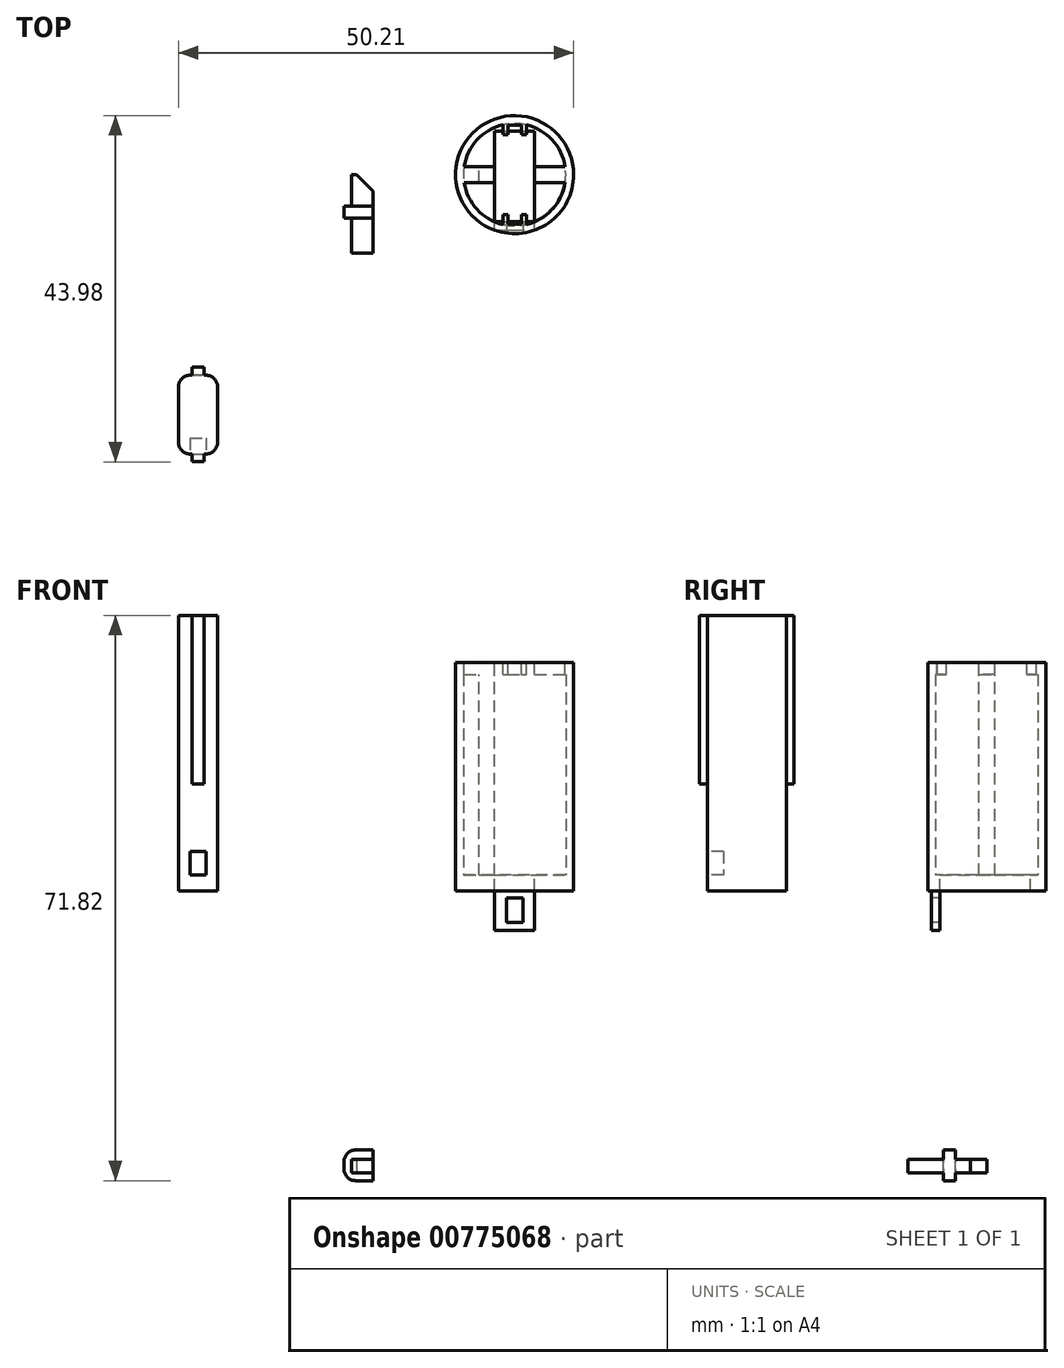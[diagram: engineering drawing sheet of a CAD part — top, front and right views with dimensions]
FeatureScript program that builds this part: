
annotation { "Feature Type Name" : "Feature", "Feature Type Description" : "" }
export const myFeature = defineFeature(function(context is Context, id is Id, definition is map)
    precondition{}
    {
        {
            var Q0;
            Q0=qCreatedBy(makeId("Top.planeOp"),FACE);
            var sketch = newSketch(context, id + "F0", { "sketchPlane" : qUnion([Q0])});
            skCircle(sketch, "E0", {"center": v(0, 0) * mm, "radius": 7.5 * mm});
            skSolve(sketch);
        }
        {
            var Q0;
            Q0=qSketchRegion(id+"F0",true);
            extrude(context, id + "F1", {"entities" : qUnion([Q0]), "depth" : 29 * mm});
        }
        {
            var Q0;
            Q0=qCreatedBy(makeId("Top.planeOp"),FACE);
            var sketch = newSketch(context, id + "F2", { "sketchPlane" : qUnion([Q0])});
            skCircle(sketch, "E1", {"center": v(0, 0) * mm, "radius": 6.5 * mm});
            skSolve(sketch);
        }
        {
            var Q0;
            Q0=makeQuery(id+"F2.imprint","IMPRINT",FACE,{"disambiguationData":[TD([[makeQuery(id+"F2.imprint","IMPRINT",EDGE,{"derivedFrom":sQuery(id+"F2.wireOp",EDGE,"E1")}),1.0]])]});
            extrude(context, id + "F3", {"entities" : qUnion([Q0]), "operationType" : NewBodyOperationType.REMOVE, "depth" : 30 * mm});
        }
        {
            var Q0;
            Q0=makeQuery(id+"F1.opExtrude","CAP_FACE",FACE,{"disambiguationData":[OSD([sQuery(id+"F0.wireOp",EDGE,"E0")])],"isStart":true});
            var sketch = newSketch(context, id + "F4", { "sketchPlane" : qUnion([Q0])});
            skCircle(sketch, "E2", {"center": v(0, 0) * mm, "radius": 6.5 * mm});
            skSolve(sketch);
        }
        {
            var Q0;
            Q0=makeQuery(id+"F4.imprint","IMPRINT",FACE,{"disambiguationData":[TD([[makeQuery(id+"F4.imprint","IMPRINT",EDGE,{"derivedFrom":sQuery(id+"F4.wireOp",EDGE,"E2")}),-1.0]])]});
            extrude(context, id + "F5", {"entities" : qUnion([Q0]), "operationType" : NewBodyOperationType.ADD, "oppositeDirection" : true, "depth" : 2 * mm});
        }
        {
            var Q0;
            Q0=qCreatedBy(makeId("Top.planeOp"),FACE);
            var sketch = newSketch(context, id + "F6", { "sketchPlane" : qUnion([Q0])});
            skLineSegment(sketch, "E3.bottom", {"start": v(-42.71, -35.48) * mm, "end": v(-40.96, -35.48) * mm});
            skLineSegment(sketch, "E3.top", {"start": v(-42.71, -25.48) * mm, "end": v(-40.96, -25.48) * mm});
            skLineSegment(sketch, "E3.left", {"start": v(-42.71, -35.48) * mm, "end": v(-42.71, -25.48) * mm});
            skLineSegment(sketch, "E3.right", {"start": v(-37.71, -35.48) * mm, "end": v(-37.71, -25.48) * mm});
            skLineSegment(sketch, "E4.top", {"start": v(-40.96, -24.48) * mm, "end": v(-39.46, -24.48) * mm});
            skLineSegment(sketch, "E4.left", {"start": v(-40.96, -25.48) * mm, "end": v(-40.96, -24.48) * mm});
            skLineSegment(sketch, "E4.right", {"start": v(-39.46, -25.48) * mm, "end": v(-39.46, -24.48) * mm});
            skLineSegment(sketch, "E5.top", {"start": v(-40.96, -36.48) * mm, "end": v(-39.46, -36.48) * mm});
            skLineSegment(sketch, "E5.left", {"start": v(-40.96, -35.48) * mm, "end": v(-40.96, -36.48) * mm});
            skLineSegment(sketch, "E5.right", {"start": v(-39.46, -35.48) * mm, "end": v(-39.46, -36.48) * mm});
            skLineSegment(sketch, "E6.trimOffspring", {"start": v(-39.46, -25.48) * mm, "end": v(-37.71, -25.48) * mm});
            skLineSegment(sketch, "E7.trimOffspring", {"start": v(-39.46, -35.48) * mm, "end": v(-37.71, -35.48) * mm});
            skSolve(sketch);
        }
        {
            var Q0;
            Q0=qSketchRegion(id+"F6",true);
            extrude(context, id + "F7", {"entities" : qUnion([Q0]), "depth" : 35 * mm});
        }
        {
            var Q0;
            Q0=makeQuery(id+"F1.opExtrude","CAP_FACE",FACE,{"disambiguationData":[OSD([sQuery(id+"F0.wireOp",EDGE,"E0")])],"isStart":false});
            var sketch = newSketch(context, id + "F8", { "sketchPlane" : qUnion([Q0])});
            skLineSegment(sketch, "E8.bottom", {"start": v(-6.5, 1) * mm, "end": v(-2.55, 1) * mm});
            skLineSegment(sketch, "E8.top", {"start": v(-6.5, -1) * mm, "end": v(-2.55, -1) * mm});
            skLineSegment(sketch, "E8.left", {"start": v(-6.5, 1) * mm, "end": v(-6.5, -1) * mm});
            skLineSegment(sketch, "E8.right", {"start": v(-2.55, 1) * mm, "end": v(-2.55, -1) * mm});
            skLineSegment(sketch, "E9.bottom", {"start": v(2.55, 1) * mm, "end": v(6.5, 1) * mm});
            skLineSegment(sketch, "E9.top", {"start": v(2.55, -1) * mm, "end": v(6.5, -1) * mm});
            skLineSegment(sketch, "E9.left", {"start": v(2.55, 1) * mm, "end": v(2.55, -1) * mm});
            skLineSegment(sketch, "E9.right", {"start": v(6.5, 1) * mm, "end": v(6.5, -1) * mm});
            skLineSegment(sketch, "E10", {"start": v(2.7, -7) * mm, "end": v(-8.3, -7) * mm});
            skPoint(sketch, "E11", {"position": v(-6.5, 0) * mm});
            skPoint(sketch, "E12", {"position": v(6.5, 0) * mm});
            skArc(sketch, "E13.trimOffspring", {"start": v(5.92, -1) * mm, "mid": v(6, 0) * mm, "end": v(5.92, 1) * mm});
            skArc(sketch, "E14.trimOffspring", {"start": v(-5.92, 1) * mm, "mid": v(-6, 0) * mm, "end": v(-5.92, -1) * mm});
            skLineSegment(sketch, "E15.bottom", {"start": v(-1.5, -6.5) * mm, "end": v(1.5, -6.5) * mm});
            skLineSegment(sketch, "E15.top", {"start": v(-1.5, -5.1) * mm, "end": v(-0.85, -5.1) * mm});
            skLineSegment(sketch, "E15.left", {"start": v(-1.5, -6.5) * mm, "end": v(-1.5, -5.1) * mm});
            skLineSegment(sketch, "E15.right", {"start": v(1.5, -6.5) * mm, "end": v(1.5, -5.1) * mm});
            skLineSegment(sketch, "E16.bottom", {"start": v(-1.5, 6.5) * mm, "end": v(1.5, 6.5) * mm});
            skLineSegment(sketch, "E16.top", {"start": v(-1.5, 5.1) * mm, "end": v(-0.85, 5.1) * mm});
            skLineSegment(sketch, "E16.left", {"start": v(-1.5, 6.5) * mm, "end": v(-1.5, 5.1) * mm});
            skLineSegment(sketch, "E16.right", {"start": v(1.5, 6.5) * mm, "end": v(1.5, 5.1) * mm});
            skPoint(sketch, "E17", {"position": v(0, 6.5) * mm});
            skPoint(sketch, "E18", {"position": v(0, -6.5) * mm});
            skLineSegment(sketch, "E19.top", {"start": v(-0.85, 6.3) * mm, "end": v(0.85, 6.3) * mm});
            skLineSegment(sketch, "E19.left", {"start": v(-0.85, 5.1) * mm, "end": v(-0.85, 6.3) * mm});
            skLineSegment(sketch, "E19.right", {"start": v(0.85, 5.1) * mm, "end": v(0.85, 6.3) * mm});
            skLineSegment(sketch, "E20.top", {"start": v(-0.85, -6.3) * mm, "end": v(0.85, -6.3) * mm});
            skLineSegment(sketch, "E20.left", {"start": v(-0.85, -5.1) * mm, "end": v(-0.85, -6.3) * mm});
            skLineSegment(sketch, "E20.right", {"start": v(0.85, -5.1) * mm, "end": v(0.85, -6.3) * mm});
            skLineSegment(sketch, "E21.trimOffspring", {"start": v(0.85, 5.1) * mm, "end": v(1.5, 5.1) * mm});
            skLineSegment(sketch, "E22.trimOffspring", {"start": v(0.85, -5.1) * mm, "end": v(1.5, -5.1) * mm});
            skSolve(sketch);
        }
        {
            var Q0;
            {var subQ4=sQuery(id+"F8.wireOp",EDGE,"E8.right");Q0=makeQuery(id+"F8.imprint","IMPRINT",FACE,{"disambiguationData":[TD([[makeQuery(id+"F8.imprint","IMPRINT",EDGE,{"derivedFrom":subQ4}),-1.0]])]});}
            var Q1;
            {var subQ1=sQuery(id+"F8.wireOp",EDGE,"XQCQReMM-DMfq-NEXw-nXjC-cKNYx5jDkKxh.top");Q1=makeQuery(id+"F8.imprint","IMPRINT",FACE,{"disambiguationData":[TD([[makeQuery(id+"F8.imprint","IMPRINT",EDGE,{"derivedFrom":subQ1}),1.0]])]});}
            var Q2;
            {var subQ0=sQuery(id+"F8.wireOp",EDGE,"E9.left");Q2=makeQuery(id+"F8.imprint","IMPRINT",FACE,{"disambiguationData":[TD([[makeQuery(id+"F8.imprint","IMPRINT",EDGE,{"derivedFrom":subQ0}),1.0]])]});}
            var Q3;
            {var subQ0=sQuery(id+"F8.wireOp",EDGE,"yVMaH1Gn-iFFF-JhyI-hApD-2K1NMgFAN3S1.top");Q3=makeQuery(id+"F8.imprint","IMPRINT",FACE,{"disambiguationData":[TD([[makeQuery(id+"F8.imprint","IMPRINT",EDGE,{"derivedFrom":subQ0}),-1.0]])]});}
            var Q4;
            {var subQ4=sQuery(id+"F8.wireOp",EDGE,"E14.trimOffspring");Q4=makeQuery(id+"F8.imprint","IMPRINT",FACE,{"disambiguationData":[TD([[makeQuery(id+"F8.imprint","IMPRINT",EDGE,{"derivedFrom":subQ4}),-1.0]])]});}
            var Q5;
            {var subQ4=sQuery(id+"F8.wireOp",EDGE,"E13.trimOffspring");Q5=makeQuery(id+"F8.imprint","IMPRINT",FACE,{"disambiguationData":[TD([[makeQuery(id+"F8.imprint","IMPRINT",EDGE,{"derivedFrom":subQ4}),-1.0]])]});}
            var Q6;
            {var subQ6=sQuery(id+"F8.wireOp",EDGE,"E16.top");Q6=makeQuery(id+"F8.imprint","IMPRINT",FACE,{"disambiguationData":[TD([[makeQuery(id+"F8.imprint","IMPRINT",EDGE,{"derivedFrom":subQ6}),1.0]])]});}
            var Q7;
            {var subQ5=sQuery(id+"F8.wireOp",EDGE,"E15.top");Q7=makeQuery(id+"F8.imprint","IMPRINT",FACE,{"disambiguationData":[TD([[makeQuery(id+"F8.imprint","IMPRINT",EDGE,{"derivedFrom":subQ5}),-1.0]])]});}
            extrude(context, id + "F9", {"entities" : qUnion([Q0, Q1, Q2, Q3, Q4, Q5, Q6, Q7]), "operationType" : NewBodyOperationType.ADD, "oppositeDirection" : true, "depth" : 1.5 * mm});
        }
        {
            var Q0;
            Q0=makeQuery(id+"F7.opExtrude","CAP_FACE",FACE,{"disambiguationData":[OSD([sQuery(id+"F6.wireOp",EDGE,"E3.bottom"),sQuery(id+"F6.wireOp",EDGE,"E3.top"),sQuery(id+"F6.wireOp",EDGE,"E3.left"),sQuery(id+"F6.wireOp",EDGE,"E3.right"),sQuery(id+"F6.wireOp",EDGE,"E4.top"),sQuery(id+"F6.wireOp",EDGE,"E4.left"),sQuery(id+"F6.wireOp",EDGE,"E4.right"),sQuery(id+"F6.wireOp",EDGE,"E5.top"),sQuery(id+"F6.wireOp",EDGE,"E5.left"),sQuery(id+"F6.wireOp",EDGE,"E5.right"),sQuery(id+"F6.wireOp",EDGE,"E6.trimOffspring"),sQuery(id+"F6.wireOp",EDGE,"E7.trimOffspring")])],"isStart":true});
            var sketch = newSketch(context, id + "F10", { "sketchPlane" : qUnion([Q0])});
            skLineSegment(sketch, "E23.bottom", {"start": v(-39.46, 24.48) * mm, "end": v(-40.96, 24.48) * mm});
            skLineSegment(sketch, "E23.top", {"start": v(-39.46, 25.48) * mm, "end": v(-40.96, 25.48) * mm});
            skLineSegment(sketch, "E23.left", {"start": v(-39.46, 24.48) * mm, "end": v(-39.46, 25.48) * mm});
            skLineSegment(sketch, "E23.right", {"start": v(-40.96, 24.48) * mm, "end": v(-40.96, 25.48) * mm});
            skLineSegment(sketch, "E24.bottom", {"start": v(-39.46, 36.48) * mm, "end": v(-40.96, 36.48) * mm});
            skLineSegment(sketch, "E24.top", {"start": v(-39.46, 35.48) * mm, "end": v(-40.96, 35.48) * mm});
            skLineSegment(sketch, "E24.left", {"start": v(-39.46, 36.48) * mm, "end": v(-39.46, 35.48) * mm});
            skLineSegment(sketch, "E24.right", {"start": v(-40.96, 36.48) * mm, "end": v(-40.96, 35.48) * mm});
            skSolve(sketch);
        }
        {
            var Q0;
            Q0=qSketchRegion(id+"F10",true);
            extrude(context, id + "F11", {"entities" : qUnion([Q0]), "operationType" : NewBodyOperationType.REMOVE, "oppositeDirection" : true, "depth" : 13.6 * mm});
        }
        {
            var Q0;
            Q0=makeQuery(id+"F5.opExtrude","CAP_FACE",FACE,{"disambiguationData":[OSD([sQuery(id+"F4.wireOp",EDGE,"E2")])],"isStart":false});
            var sketch = newSketch(context, id + "F12", { "sketchPlane" : qUnion([Q0])});
            skLineSegment(sketch, "E25.0", {"start": v(-2.55, 1) * mm, "end": v(-2.55, -1) * mm});
            skLineSegment(sketch, "E26.0", {"start": v(-1, 5.55) * mm, "end": v(-0.3, 5.55) * mm});
            skLineSegment(sketch, "E27.0", {"start": v(2.55, 1) * mm, "end": v(2.55, -1) * mm});
            skLineSegment(sketch, "E28.0", {"start": v(-1, -5.55) * mm, "end": v(-0.3, -5.55) * mm});
            skPoint(sketch, "E29.firstSnap0", {"position": v(-0.65, 5.55) * mm});
            skPoint(sketch, "E29.firstSnap1", {"position": v(-2.55, 0) * mm});
            skPoint(sketch, "E29.oppositeSnap0", {"position": v(2.55, 0) * mm});
            skLineSegment(sketch, "E29.bottom", {"start": v(-2.55, 5.55) * mm, "end": v(2.55, 5.55) * mm});
            skLineSegment(sketch, "E29.top", {"start": v(-2.55, -5.98) * mm, "end": v(2.55, -5.98) * mm});
            skLineSegment(sketch, "E29.left", {"start": v(-2.55, 5.55) * mm, "end": v(-2.55, -5.98) * mm});
            skLineSegment(sketch, "E29.right", {"start": v(2.55, 5.55) * mm, "end": v(2.55, -5.98) * mm});
            skSolve(sketch);
        }
        {
            var Q0;
            Q0=qSketchRegion(id+"F12",true);
            extrude(context, id + "F13", {"entities" : qUnion([Q0]), "operationType" : NewBodyOperationType.REMOVE, "oppositeDirection" : true, "depth" : 25 * mm});
        }
        {
            var Q0;
            Q0=makeQuery(id+"F7.opExtrude","SWEPT_EDGE",EDGE,{"disambiguationData":[OSD([sQuery(id+"F6.wireOp",EDGE,"E3.top"),sQuery(id+"F6.wireOp",EDGE,"E3.left")])]});
            var Q1;
            Q1=makeQuery(id+"F7.opExtrude","SWEPT_EDGE",EDGE,{"disambiguationData":[OSD([sQuery(id+"F6.wireOp",EDGE,"E3.right"),sQuery(id+"F6.wireOp",EDGE,"E6.trimOffspring")])]});
            var Q2;
            Q2=makeQuery(id+"F7.opExtrude","SWEPT_EDGE",EDGE,{"disambiguationData":[OSD([sQuery(id+"F6.wireOp",EDGE,"E3.right"),sQuery(id+"F6.wireOp",EDGE,"E7.trimOffspring")])]});
            var Q3;
            Q3=makeQuery(id+"F7.opExtrude","SWEPT_EDGE",EDGE,{"disambiguationData":[OSD([sQuery(id+"F6.wireOp",EDGE,"E3.bottom"),sQuery(id+"F6.wireOp",EDGE,"E3.left")])]});
            fillet(context, id + "F14", {"entities" : qUnion([Q0, Q1, Q2, Q3]), "radius" : 1.5 * mm, "tangentPropagation" : true, "allowEdgeOverflow" : false});
        }
        {
            var Q0;
            Q0=makeQuery(id+"F11.boolean.opBoolean","MERGE",FACE,{"derivedFrom":[makeQuery(id+"F7.opExtrude","SWEPT_FACE",FACE,{"disambiguationData":[OSD([sQuery(id+"F6.wireOp",EDGE,"E3.bottom")])]}),makeQuery(id+"F7.opExtrude","SWEPT_FACE",FACE,{"disambiguationData":[OSD([sQuery(id+"F6.wireOp",EDGE,"E7.trimOffspring")])]}),makeQuery(id+"F11.opExtrude","SWEPT_FACE",FACE,{"disambiguationData":[OSD([sQuery(id+"F10.wireOp",EDGE,"E24.top")])]})]});
            var sketch = newSketch(context, id + "F15", { "sketchPlane" : qUnion([Q0])});
            skLineSegment(sketch, "E30", {"start": v(-40.21, 0) * mm, "end": v(-40.21, 6) * mm});
            skLineSegment(sketch, "E31.bottom", {"start": v(-41.21, 2) * mm, "end": v(-39.21, 2) * mm});
            skLineSegment(sketch, "E31.top", {"start": v(-41.21, 5) * mm, "end": v(-39.21, 5) * mm});
            skLineSegment(sketch, "E31.left", {"start": v(-41.21, 2) * mm, "end": v(-41.21, 5) * mm});
            skLineSegment(sketch, "E31.right", {"start": v(-39.21, 2) * mm, "end": v(-39.21, 5) * mm});
            skSolve(sketch);
        }
        {
            var Q0;
            Q0=qSketchRegion(id+"F15",true);
            extrude(context, id + "F16", {"entities" : qUnion([Q0]), "operationType" : NewBodyOperationType.REMOVE, "oppositeDirection" : true, "depth" : 2 * mm});
        }
        {
            var Q0;
            Q0=makeQuery(id+"F5.boolean.opBoolean","MERGE",FACE,{"derivedFrom":[makeQuery(id+"F1.opExtrude","CAP_FACE",FACE,{"disambiguationData":[OSD([sQuery(id+"F0.wireOp",EDGE,"E0")])],"isStart":true}),makeQuery(id+"F5.opExtrude","CAP_FACE",FACE,{"disambiguationData":[OSD([sQuery(id+"F4.wireOp",EDGE,"E2")])],"isStart":true})]});
            var sketch = newSketch(context, id + "F17", { "sketchPlane" : qUnion([Q0])});
            skLineSegment(sketch, "E32.bottom", {"start": v(-2.55, 7.05) * mm, "end": v(2.55, 7.05) * mm});
            skLineSegment(sketch, "E32.top", {"start": v(-2.55, 5.98) * mm, "end": v(2.55, 5.98) * mm});
            skLineSegment(sketch, "E32.left", {"start": v(-2.55, 7.05) * mm, "end": v(-2.55, 5.98) * mm});
            skLineSegment(sketch, "E32.right", {"start": v(2.55, 7.05) * mm, "end": v(2.55, 5.98) * mm});
            skSolve(sketch);
        }
        {
            var Q0;
            Q0=makeQuery(id+"F17.imprint","IMPRINT",FACE,{"disambiguationData":[TD([[makeQuery(id+"F17.imprint","IMPRINT",EDGE,{"derivedFrom":sQuery(id+"F17.wireOp",EDGE,"E32.bottom")}),-1.0]])]});
            extrude(context, id + "F18", {"entities" : qUnion([Q0]), "operationType" : NewBodyOperationType.ADD, "depth" : 5 * mm});
        }
        {
            var Q0;
            Q0=makeQuery(id+"F18.opExtrude","SWEPT_FACE",FACE,{"disambiguationData":[OSD([sQuery(id+"F17.wireOp",EDGE,"E32.bottom")])]});
            var sketch = newSketch(context, id + "F19", { "sketchPlane" : qUnion([Q0])});
            skLineSegment(sketch, "E33.bottom", {"start": v(-1.05, -4) * mm, "end": v(1.05, -4) * mm});
            skLineSegment(sketch, "E33.top", {"start": v(-1.05, -0.9) * mm, "end": v(1.05, -0.9) * mm});
            skLineSegment(sketch, "E33.left", {"start": v(-1.05, -4) * mm, "end": v(-1.05, -0.9) * mm});
            skLineSegment(sketch, "E33.right", {"start": v(1.05, -4) * mm, "end": v(1.05, -0.9) * mm});
            skSolve(sketch);
        }
        {
            var Q0;
            Q0=qSketchRegion(id+"F19",true);
            extrude(context, id + "F20", {"entities" : qUnion([Q0]), "operationType" : NewBodyOperationType.REMOVE, "oppositeDirection" : true, "depth" : 25 * mm});
        }
        {
            var Q0;
            Q0=qCreatedBy(makeId("Front.planeOp"),FACE);
            var sketch = newSketch(context, id + "F21", { "sketchPlane" : qUnion([Q0])});
            skLineSegment(sketch, "E34.bottom", {"start": v(-20.69, -35.82) * mm, "end": v(-17.99, -35.82) * mm});
            skLineSegment(sketch, "E34.top", {"start": v(-20.69, -34.12) * mm, "end": v(-17.99, -34.12) * mm});
            skLineSegment(sketch, "E34.left", {"start": v(-20.69, -35.82) * mm, "end": v(-20.69, -34.12) * mm});
            skLineSegment(sketch, "E34.right", {"start": v(-17.99, -35.82) * mm, "end": v(-17.99, -34.12) * mm});
            skSolve(sketch);
        }
        {
            var Q0;
            Q0=qSketchRegion(id+"F21",true);
            extrude(context, id + "F22", {"entities" : qUnion([Q0]), "depth" : 10 * mm});
        }
        {
            var Q0;
            Q0=makeQuery(id+"F22.opExtrude","SWEPT_FACE",FACE,{"disambiguationData":[OSD([sQuery(id+"F21.wireOp",EDGE,"E34.bottom")])]});
            var sketch = newSketch(context, id + "F23", { "sketchPlane" : qUnion([Q0])});
            skLineSegment(sketch, "E35", {"start": v(-17.99, 2.1) * mm, "end": v(-20.09, 0) * mm});
            skLineSegment(sketch, "E36", {"start": v(-20.09, 0) * mm, "end": v(-17.99, 0) * mm});
            skLineSegment(sketch, "E37", {"start": v(-17.99, 0) * mm, "end": v(-17.99, 2.1) * mm});
            skSolve(sketch);
        }
        {
            var Q0;
            Q0=qSketchRegion(id+"F23",true);
            extrude(context, id + "F24", {"entities" : qUnion([Q0]), "operationType" : NewBodyOperationType.REMOVE, "oppositeDirection" : true, "depth" : 25 * mm});
        }
        {
            var Q0;
            Q0=makeQuery(id+"F9.opExtrude","CAP_FACE",FACE,{"disambiguationData":[OSD([sQuery(id+"F8.wireOp",EDGE,"E8.bottom"),sQuery(id+"F8.wireOp",EDGE,"E8.top"),sQuery(id+"F8.wireOp",EDGE,"E8.right"),sQuery(id+"F8.wireOp",EDGE,"1d744317-5d0a-47f8-8d17-6fdc50faddf4.0")])],"isStart":false});
            var sketch = newSketch(context, id + "F25", { "sketchPlane" : qUnion([Q0])});
            skLineSegment(sketch, "E38.bottom", {"start": v(-4.55, 1) * mm, "end": v(-2.55, 1) * mm});
            skLineSegment(sketch, "E38.top", {"start": v(-4.55, -1) * mm, "end": v(-2.55, -1) * mm});
            skLineSegment(sketch, "E38.left", {"start": v(-4.55, 1) * mm, "end": v(-4.55, -1) * mm});
            skLineSegment(sketch, "E38.right", {"start": v(-2.55, 1) * mm, "end": v(-2.55, -1) * mm});
            skLineSegment(sketch, "E39.0.0", {"start": v(2.55, 1) * mm, "end": v(2.55, -1) * mm});
            skLineSegment(sketch, "E39.0.1", {"start": v(2.55, -1) * mm, "end": v(2.55, -1) * mm});
            skLineSegment(sketch, "E39.0.3", {"start": v(5.92, 1) * mm, "end": v(2.55, 1) * mm});
            skLineSegment(sketch, "E40.bottom", {"start": v(4.55, 1) * mm, "end": v(2.55, 1) * mm});
            skLineSegment(sketch, "E40.top", {"start": v(4.55, -1) * mm, "end": v(2.55, -1) * mm});
            skLineSegment(sketch, "E40.left", {"start": v(4.55, 1) * mm, "end": v(4.55, -1) * mm});
            skSolve(sketch);
        }
        {
            var Q0;
            Q0=makeQuery(id+"F25.imprint","IMPRINT",FACE,{"disambiguationData":[TD([[makeQuery(id+"F25.imprint","IMPRINT",EDGE,{"derivedFrom":sQuery(id+"F25.wireOp",EDGE,"E40.bottom")}),1.0]])]});
            var Q1;
            Q1=makeQuery(id+"F25.imprint","IMPRINT",FACE,{"disambiguationData":[TD([[makeQuery(id+"F25.imprint","IMPRINT",EDGE,{"derivedFrom":sQuery(id+"F25.wireOp",EDGE,"E38.bottom")}),-1.0]])]});
            var Q2;
            {var subQ0=makeQuery(id+"F5.opExtrude","CAP_FACE",FACE,{"disambiguationData":[OSD([sQuery(id+"F4.wireOp",EDGE,"E2")])],"isStart":false});Q2=makeQuery(id+"F13.boolean.opBoolean","SPLIT",FACE,{"disambiguationData":[TD([makeQuery(id+"F3.boolean.opBoolean","COPY",FACE,{"derivedFrom":makeQuery(id+"F3.opExtrude","SWEPT_FACE",FACE,{"disambiguationData":[OSD([sQuery(id+"F2.wireOp",EDGE,"E1")])]})}),subQ0,makeQuery(id+"F13.opExtrude","SWEPT_FACE",FACE,{"disambiguationData":[OSD([sQuery(id+"F12.wireOp",EDGE,"E29.bottom")])]}),makeQuery(id+"F13.opExtrude","SWEPT_FACE",FACE,{"disambiguationData":[OSD([sQuery(id+"F12.wireOp",EDGE,"E29.top")])]}),makeQuery(id+"F13.opExtrude","SWEPT_FACE",FACE,{"disambiguationData":[OSD([sQuery(id+"F12.wireOp",EDGE,"E29.left")])]}),makeQuery(id+"F13.opExtrude","SWEPT_FACE",FACE,{"disambiguationData":[OSD([sQuery(id+"F12.wireOp",EDGE,"E29.right")])]})])],"derivedFrom":subQ0});}
            extrude(context, id + "F26", {"entities" : qUnion([Q0, Q1]), "operationType" : NewBodyOperationType.ADD, "endBound" : BoundingType.UP_TO_SURFACE, "endBoundEntityFace" : qUnion([Q2]), "depth" : 25 * mm});
        }
        {
            var Q0;
            Q0=makeQuery(id+"F22.opExtrude","SWEPT_FACE",FACE,{"disambiguationData":[OSD([sQuery(id+"F21.wireOp",EDGE,"E34.bottom")])]});
            var sketch = newSketch(context, id + "F27", { "sketchPlane" : qUnion([Q0])});
            skLineSegment(sketch, "E41.bottom", {"start": v(-21.69, 4) * mm, "end": v(-17.99, 4) * mm});
            skLineSegment(sketch, "E41.top", {"start": v(-21.69, 5.5) * mm, "end": v(-17.99, 5.5) * mm});
            skLineSegment(sketch, "E41.left", {"start": v(-21.69, 4) * mm, "end": v(-21.69, 5.5) * mm});
            skLineSegment(sketch, "E41.right", {"start": v(-17.99, 4) * mm, "end": v(-17.99, 5.5) * mm});
            skSolve(sketch);
        }
        {
            var Q0;
            Q0=qSketchRegion(id+"F27",true);
            extrude(context, id + "F28", {"entities" : qUnion([Q0]), "operationType" : NewBodyOperationType.ADD, "depth" : 1 * mm, "hasSecondDirection" : true, "secondDirectionOppositeDirection" : true, "secondDirectionDepth" : 2.9 * mm});
        }
        {
            var Q0;
            Q0=makeQuery(id+"F28.opExtrude","CAP_EDGE",EDGE,{"disambiguationData":[OSD([sQuery(id+"F27.wireOp",EDGE,"E41.left")])],"isStart":false});
            var Q1;
            Q1=makeQuery(id+"F28.opExtrude","CAP_EDGE",EDGE,{"disambiguationData":[OSD([sQuery(id+"F27.wireOp",EDGE,"E41.left")])],"isStart":true});
            fillet(context, id + "F29", {"entities" : qUnion([Q0, Q1]), "radius" : 1.5 * mm, "tangentPropagation" : true, "allowEdgeOverflow" : false});
        }
    });
